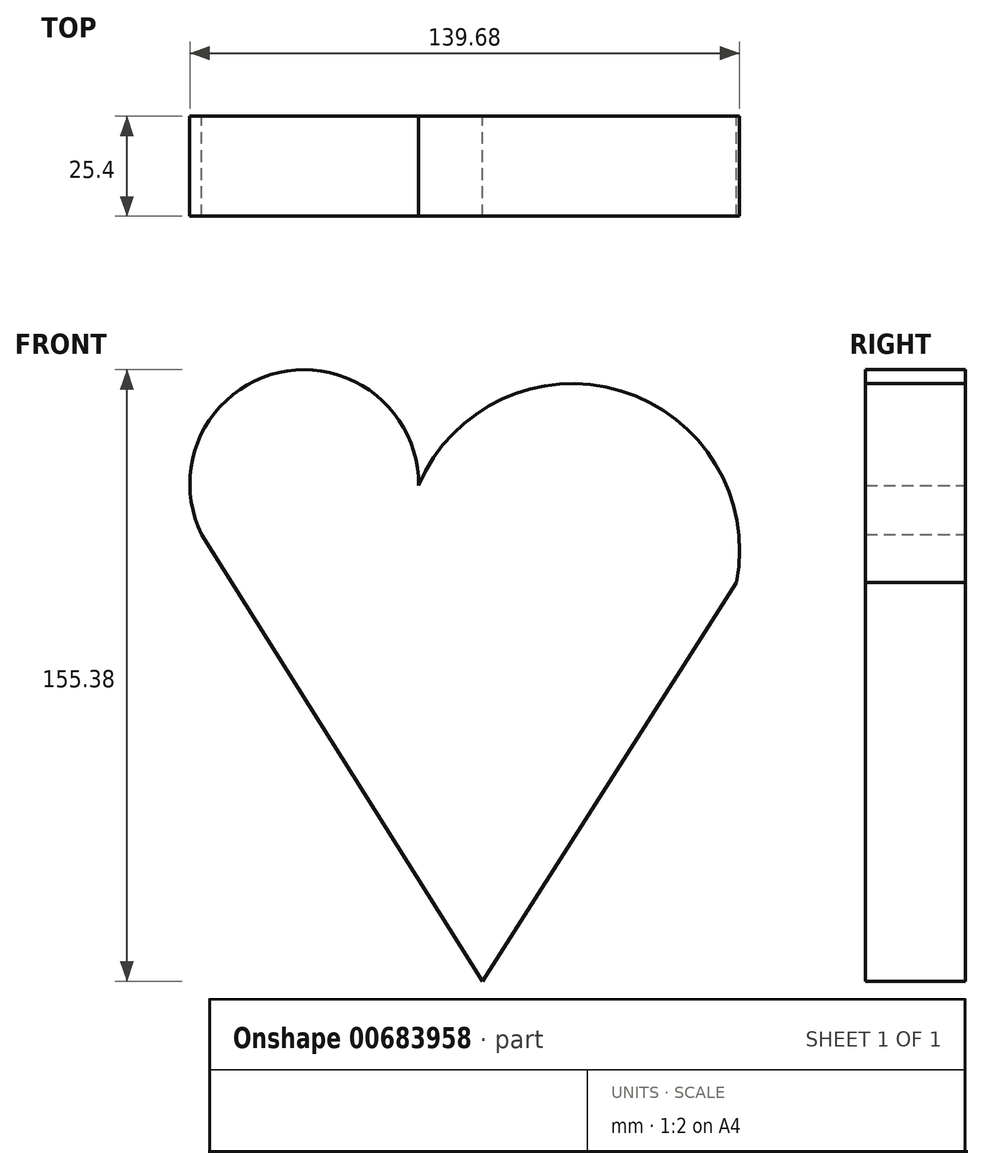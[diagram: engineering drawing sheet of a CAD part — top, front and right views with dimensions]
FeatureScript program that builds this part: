
annotation { "Feature Type Name" : "Feature", "Feature Type Description" : "" }
export const myFeature = defineFeature(function(context is Context, id is Id, definition is map)
    precondition{}
    {
        {
            var Q0;
            Q0=qCreatedBy(makeId("Front.planeOp"),FACE);
            var sketch = newSketch(context, id + "F0", { "sketchPlane" : qUnion([Q0])});
            skLineSegment(sketch, "E0", {"start": v(-29.8, 33.9) * mm, "end": v(-29.8, 78.8) * mm});
            skLineSegment(sketch, "E1", {"start": v(-29.8, 78.8) * mm, "end": v(-29.8, 78.8) * mm});
            skLineSegment(sketch, "E2", {"start": v(-29.8, 78.8) * mm, "end": v(-29.8, 82.1) * mm});
            skArc(sketch, "E3", {"start": v(-29.9, 76.6) * mm, "mid": v(-64.24, 107.65) * mm, "end": v(-84.91, 66.24) * mm});
            skArc(sketch, "E4", {"start": v(51.01, 54.16) * mm, "mid": v(21.67, 102.78) * mm, "end": v(-29.8, 78.8) * mm});
            skLineSegment(sketch, "E5", {"start": v(-84.91, 66.24) * mm, "end": v(-13.51, -47.22) * mm});
            skLineSegment(sketch, "E6", {"start": v(-13.51, -47.22) * mm, "end": v(51.01, 54.16) * mm});
            skSolve(sketch);
        }
        {
            var Q0;
            Q0 = qSketchRegion(id + "F0", true);
            extrude(context, id + "F1", {"entities" : qUnion([Q0]), "depth" : 25.4 * mm, "offsetDistance" : 25.4 * mm});
        }
    });
